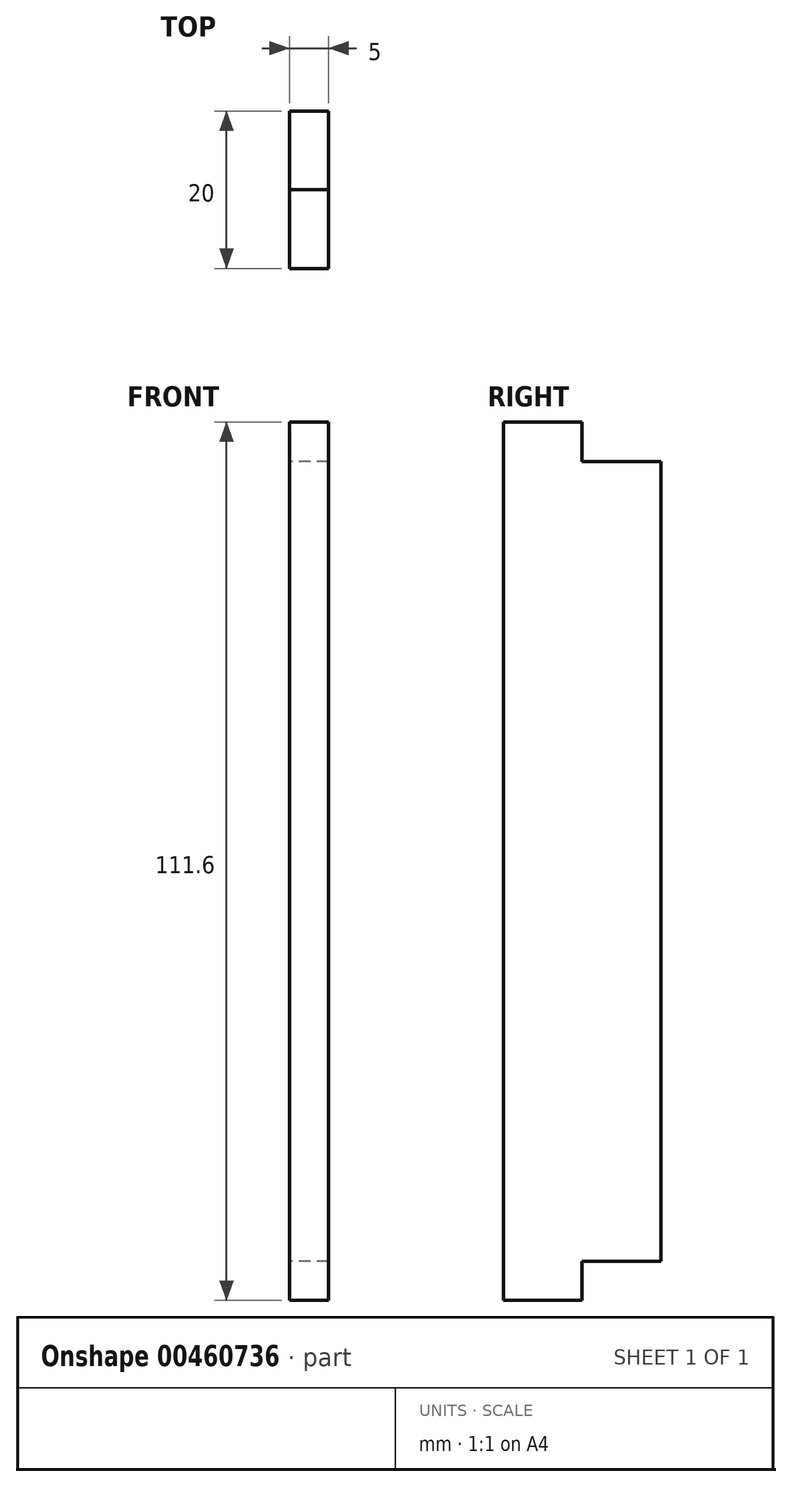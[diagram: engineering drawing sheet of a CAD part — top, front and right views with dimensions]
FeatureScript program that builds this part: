
annotation { "Feature Type Name" : "Feature", "Feature Type Description" : "" }
export const myFeature = defineFeature(function(context is Context, id is Id, definition is map)
    precondition{}
    {
        {
            var Q0;
            Q0=qCreatedBy(makeId("Right.planeOp"),FACE);
            var sketch = newSketch(context, id + "F0", { "sketchPlane" : qUnion([Q0])});
            skLineSegment(sketch, "E0", {"start": v(0, 0) * mm, "end": v(0, -101.6) * mm});
            skLineSegment(sketch, "E1", {"start": v(0, -101.6) * mm, "end": v(-10, -101.6) * mm});
            skLineSegment(sketch, "E2", {"start": v(-10, -101.6) * mm, "end": v(-10, -106.6) * mm});
            skLineSegment(sketch, "E3", {"start": v(-10, -106.6) * mm, "end": v(-20, -106.6) * mm});
            skLineSegment(sketch, "E4", {"start": v(-20, -106.6) * mm, "end": v(-20, -101.6) * mm});
            skLineSegment(sketch, "E5", {"start": v(-20, -101.6) * mm, "end": v(-20, 0) * mm});
            skLineSegment(sketch, "E6", {"start": v(-20, 0) * mm, "end": v(-20, 5) * mm});
            skLineSegment(sketch, "E7", {"start": v(-20, 5) * mm, "end": v(-10, 5) * mm});
            skLineSegment(sketch, "E8", {"start": v(-10, 5) * mm, "end": v(-10, 0) * mm});
            skLineSegment(sketch, "E9", {"start": v(-10, 0) * mm, "end": v(0, 0) * mm});
            skPoint(sketch, "E10", {"position": v(0, 5) * mm});
            skSolve(sketch);
        }
        {
            var Q0;
            Q0 = qSketchRegion(id + "F0", true);
            extrude(context, id + "F1", {"entities" : qUnion([Q0]), "depth" : 5 * mm});
        }
    });
